# Revit family: Drain_Floor_Round_Shallow-Zurn-ZPD1-LR
name_source: partatom
category: Plumbing Fixtures
units: mm (PartAtom-declared; Revit-internal decimal feet)

## family parameters
Always vertical = Yes
Cut with Voids When Loaded = No
Maintain Annotation Orientation = No
OmniClass Number = 23.70.50.21.24.14
OmniClass Title = Deck Waste Water Drains
Part Type = Normal
Room Calculation Point = No
Round Connector Dimension = Use Radius
Shared = No
Work Plane-Based = No

## types (4) — shared parameters
Assembly Code = D2030300
Body Height (E) = 12.156 "
CW Connection = No
Default Elevation = 20 "
Description = ZURN POD PRO SHALLOW FLOOR DRAIN WITH “TYPE LR” LIGATURE RESISTANT STRAINER
HW Connection = No
Manufacturer = Zurn Water, LLC
Manufacurer Brand = Zurn
Material Main = Steel - Zurn - Stainless - Type - 304
Model = ZPD1-LR
Modified Date = 02/19/2026
Product Documentation Link = https://files.zurn.com
Product Installation Sheet URL = https://files.zurn.com
Product Page URL = https://www.zurn.com
Product data url = https://bimobject.com
Strainer Material = Steel - Zurn - Stainless - Type - 304
Strainer Open Area = 1.9 in²
URL = www.zurn.com
Vent Connection = No
WFU = 1
Waste Connection = Yes
zero-valued in all types: CWFU, HWFU

## per-type parameters (varying)
| type | Approx. Wt. Lbs. | Grate Radius | Pipe Size 'A' (Inner Diameter) | Pipe Size 'A' (Inner Radius) | Pipe Size 'A' (Nominal Diameter) | Pipe Size 'A' (Nominal Radius) | Pipe Size 'A' (Outer Diameter) | Pipe Size 'A' (Outer Radius) | Strainer Diameter (B) | Strainer Radius |
| ZPD1-LR with 6 Inch Strainer and 3 Inch No-Hub Outlet | 6.90 lb | 2.7 " | 3.068 " | 1.534 " | 3 " | 1.5 " | 3.5 " | 1.75 " | 6 " | 3 " |
| ZPD1-LR with 5 Inch Strainer and 2 Inch No-Hub Outlet | 5.30 lb | 2.2 " | 2.067 " | 1.034 " | 2 " | 1 " | 2.375 " | 1.188 " | 5 " | 2.5 " |
| ZPD1-LR with 5 Inch Strainer and 3 Inch No-Hub Outlet | 5.30 lb | 2.2 " | 3.068 " | 1.534 " | 3 " | 1.5 " | 3.5 " | 1.75 " | 5 " | 2.5 " |
| ZPD1-LR with 6 Inch Strainer and 2 Inch No-Hub Outlet | 6.90 lb | 2.7 " | 2.067 " | 1.034 " | 2 " | 1 " | 2.375 " | 1.188 " | 6 " | 3 " |

## geometry (parser evidence)
native form markers: Sweep x11
no freeform markers — native parametric forms only
